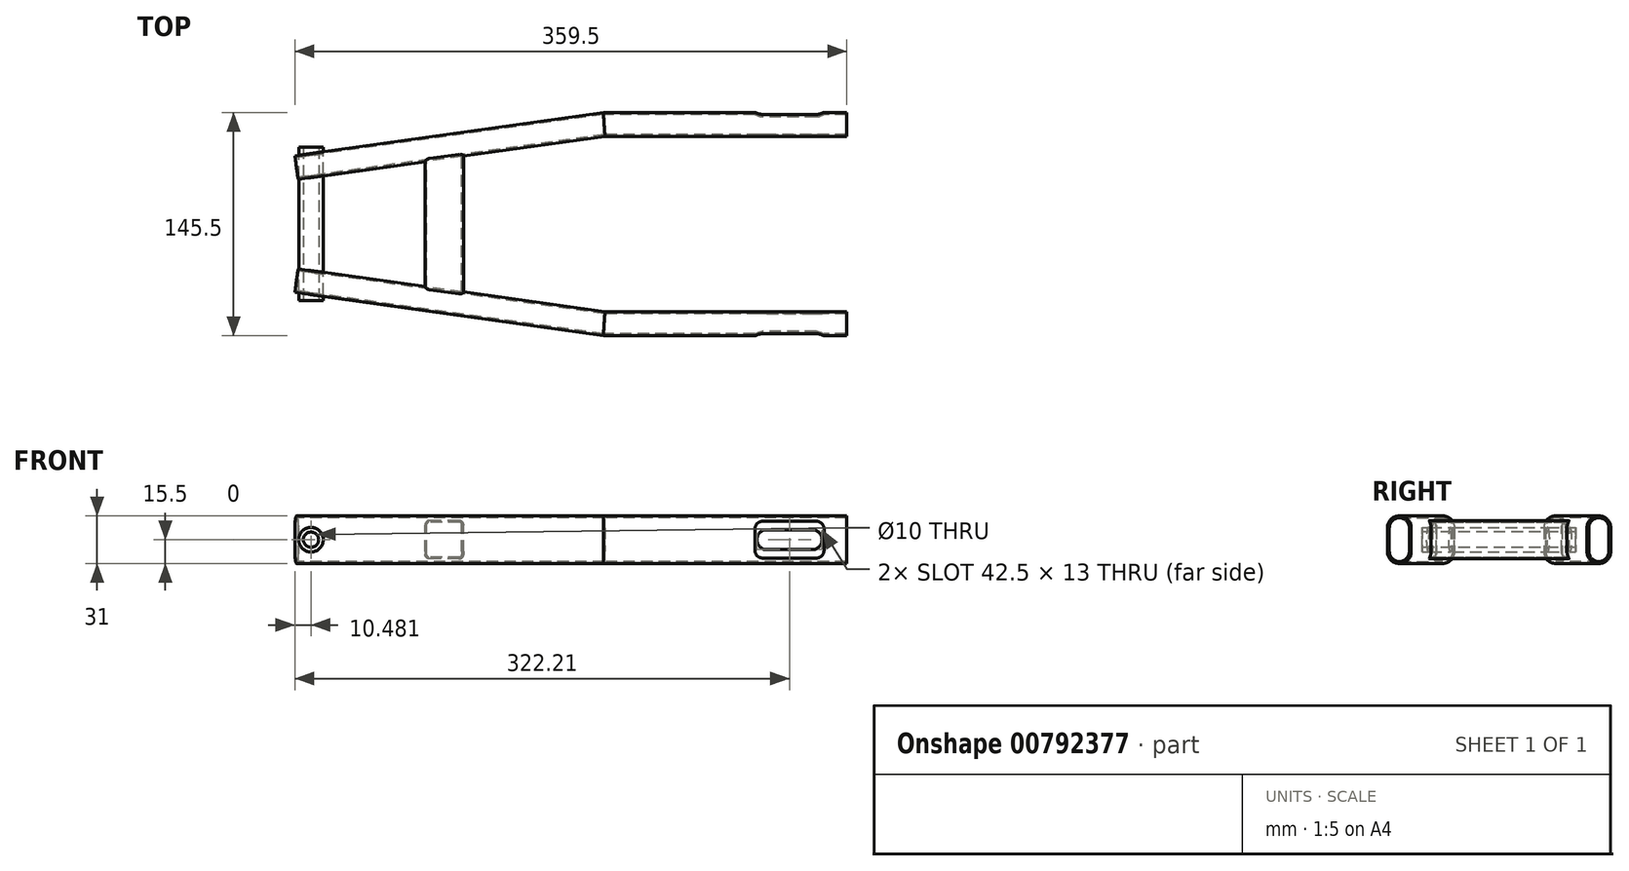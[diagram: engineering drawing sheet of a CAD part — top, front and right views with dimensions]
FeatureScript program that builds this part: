
annotation { "Feature Type Name" : "Feature", "Feature Type Description" : "" }
export const myFeature = defineFeature(function(context is Context, id is Id, definition is map)
    precondition{}
    {
        {
            var Q0;
            Q0=qCreatedBy(makeId("Top.planeOp"),FACE);
            var sketch = newSketch(context, id + "F0", { "sketchPlane" : qUnion([Q0])});
            skLineSegment(sketch, "E0", {"start": v(0, 65) * mm, "end": v(-158.03, 65) * mm});
            skLineSegment(sketch, "E1", {"start": v(-158.03, 65) * mm, "end": v(-358.42, 36.84) * mm});
            skSolve(sketch);
        }
        {
            var Q0;
            Q0=qCreatedBy(makeId("Right.planeOp"),FACE);
            var sketch = newSketch(context, id + "F1", { "sketchPlane" : qUnion([Q0])});
            skLineSegment(sketch, "E2.bottom", {"start": v(57.25, 7.75) * mm, "end": v(72.75, 7.75) * mm});
            skLineSegment(sketch, "E2.top", {"start": v(57.25, -7.75) * mm, "end": v(72.75, -7.75) * mm});
            skLineSegment(sketch, "E2.left", {"start": v(57.25, 7.75) * mm, "end": v(57.25, -7.75) * mm});
            skLineSegment(sketch, "E2.right", {"start": v(72.75, 7.75) * mm, "end": v(72.75, -7.75) * mm});
            skPoint(sketch, "E2.middle", {"position": v(65, 0) * mm});
            skArc(sketch, "E3", {"start": v(57.25, 7.75) * mm, "mid": v(65, 15.5) * mm, "end": v(72.75, 7.75) * mm});
            skArc(sketch, "E4", {"start": v(72.75, -7.75) * mm, "mid": v(65, -15.5) * mm, "end": v(57.25, -7.75) * mm});
            skLineSegment(sketch, "E5.0", {"start": v(58.45, 7.75) * mm, "end": v(58.45, -7.75) * mm});
            skLineSegment(sketch, "E6.0", {"start": v(71.55, 7.75) * mm, "end": v(71.55, -7.75) * mm});
            skArc(sketch, "E7.0", {"start": v(58.45, 7.75) * mm, "mid": v(65, 14.3) * mm, "end": v(71.55, 7.75) * mm});
            skArc(sketch, "E8.0", {"start": v(71.55, -7.75) * mm, "mid": v(65, -14.3) * mm, "end": v(58.45, -7.75) * mm});
            skSolve(sketch);
        }
        {
            var Q0;
            Q0 = qSketchRegion(id + "F1", true);
            var Q1;
            Q1 = qConstructionFilter(qBodyType(qCreatedBy(id + "F0" ,EDGE), BodyType.WIRE), ConstructionObject.NO);
            sweep(context, id + "F2", {"profiles" : qUnion([Q0]), "path" : qUnion([Q1])});
        }
        {
            var Q0;
            Q0=makeQuery(id+"F2.opSweep","SWEPT_FACE",FACE,{"disambiguationData":[OSD([sQuery(id+"F0.wireOp",EDGE,"E0"),sQuery(id+"F1.wireOp",EDGE,"E2.left")])]});
            var sketch = newSketch(context, id + "F3", { "sketchPlane" : qUnion([Q0])});
            skLineSegment(sketch, "E9.bottom", {"start": v(-22.54, -6.5) * mm, "end": v(-52.04, -6.5) * mm});
            skLineSegment(sketch, "E9.top", {"start": v(-22.54, 6.5) * mm, "end": v(-52.04, 6.5) * mm});
            skPoint(sketch, "E9.middle", {"position": v(-37.29, 0) * mm});
            skArc(sketch, "E10", {"start": v(-52.04, 6.5) * mm, "mid": v(-58.54, 0) * mm, "end": v(-52.04, -6.5) * mm});
            skArc(sketch, "E11", {"start": v(-22.54, 6.5) * mm, "mid": v(-16.04, 0) * mm, "end": v(-22.54, -6.5) * mm});
            skSolve(sketch);
        }
        {
            var Q0;
            Q0 = qSketchRegion(id + "F3", true);
            extrude(context, id + "F4", {"entities" : qUnion([Q0]), "operationType" : NewBodyOperationType.REMOVE, "oppositeDirection" : true, "depth" : 2 * mm, "offsetDistance" : 25 * mm});
        }
        {
            var Q0;
            Q0=makeQuery(id+"F2.opSweep","SWEPT_BODY",BODY,{"disambiguationData":[OSD([sQuery(id+"F0.wireOp",EDGE,"E1"),sQuery(id+"F1.wireOp",EDGE,"E2.left"),sQuery(id+"F1.wireOp",EDGE,"E2.right"),sQuery(id+"F1.wireOp",EDGE,"E3"),sQuery(id+"F1.wireOp",EDGE,"E4"),sQuery(id+"F1.wireOp",EDGE,"E5.0"),sQuery(id+"F1.wireOp",EDGE,"E6.0"),sQuery(id+"F1.wireOp",EDGE,"E7.0"),sQuery(id+"F1.wireOp",EDGE,"E8.0")])]});
            var Q1;
            Q1=qCreatedBy(makeId("Front.planeOp"),FACE);
            mirror(context, id + "F5", {"entities" : qUnion([Q0]), "mirrorPlane" : qUnion([Q1])});
        }
        {
            var Q0;
            Q0=makeQuery(id+"F5.opPattern","COPY",FACE,{"derivedFrom":makeQuery(id+"F2.opSweep","SWEPT_FACE",FACE,{"disambiguationData":[OSD([sQuery(id+"F0.wireOp",EDGE,"E0"),sQuery(id+"F1.wireOp",EDGE,"E2.right")])]}),"instanceName":"1"});
            var sketch = newSketch(context, id + "F6", { "sketchPlane" : qUnion([Q0])});
            skLineSegment(sketch, "E12.bottom", {"start": v(-19.76, 12) * mm, "end": v(-54.76, 12) * mm});
            skLineSegment(sketch, "E12.top", {"start": v(-19.76, -12) * mm, "end": v(-54.76, -12) * mm});
            skLineSegment(sketch, "E12.left", {"start": v(-14.76, 7) * mm, "end": v(-14.76, -7) * mm});
            skLineSegment(sketch, "E12.right", {"start": v(-59.76, 7) * mm, "end": v(-59.76, -7) * mm});
            skPoint(sketch, "E12.middle", {"position": v(-37.26, 0) * mm});
            skPoint(sketch, "E13.visualSharp", {"position": v(-59.76, 12) * mm});
            skArc(sketch, "E13.filletArc", {"start": v(-54.76, 12) * mm, "mid": v(-58.3, 10.54) * mm, "end": v(-59.76, 7) * mm});
            skPoint(sketch, "E14.visualSharp", {"position": v(-59.76, -12) * mm});
            skArc(sketch, "E14.filletArc", {"start": v(-59.76, -7) * mm, "mid": v(-58.3, -10.54) * mm, "end": v(-54.76, -12) * mm});
            skPoint(sketch, "E15.visualSharp", {"position": v(-14.76, -12) * mm});
            skArc(sketch, "E15.filletArc", {"start": v(-19.76, -12) * mm, "mid": v(-16.22, -10.54) * mm, "end": v(-14.76, -7) * mm});
            skPoint(sketch, "E16.visualSharp", {"position": v(-14.76, 12) * mm});
            skArc(sketch, "E16.filletArc", {"start": v(-14.76, 7) * mm, "mid": v(-16.22, 10.54) * mm, "end": v(-19.76, 12) * mm});
            skCircle(sketch, "E17", {"center": v(-349.02, 0) * mm, "radius": 8 * mm});
            skCircle(sketch, "E18", {"center": v(-349.02, 0) * mm, "radius": 5 * mm});
            skSolve(sketch);
        }
        {
            var Q0;
            {var subQ0=sQuery(id+"F6.wireOp",EDGE,"E12.bottom");Q0=makeQuery(id+"F6.imprint","IMPRINT",FACE,{"disambiguationData":[TD([[makeQuery(id+"F6.imprint","IMPRINT",EDGE,{"derivedFrom":subQ0}),1.0]])]});}
            var Q1;
            {var subQ9=sQuery(id+"F6.wireOp",EDGE,"E12.left");Q1=makeQuery(id+"F6.imprint","IMPRINT",FACE,{"disambiguationData":[TD([[makeQuery(id+"F6.imprint","IMPRINT",EDGE,{"derivedFrom":subQ9}),-1.0]])]});}
            var Q2;
            {var subQ0=sQuery(id+"F6.wireOp",EDGE,"E12.top");Q2=makeQuery(id+"F6.imprint","IMPRINT",FACE,{"disambiguationData":[TD([[makeQuery(id+"F6.imprint","IMPRINT",EDGE,{"derivedFrom":subQ0}),-1.0]])]});}
            extrude(context, id + "F7", {"entities" : qUnion([Q0, Q1, Q2]), "operationType" : NewBodyOperationType.REMOVE, "oppositeDirection" : true, "depth" : 5 * mm, "offsetDistance" : 25 * mm});
        }
        {
            var Q0;
            Q0=makeQuery(id+"F2.opSweep","SWEPT_FACE",FACE,{"disambiguationData":[OSD([sQuery(id+"F0.wireOp",EDGE,"E0"),sQuery(id+"F1.wireOp",EDGE,"E2.right")])]});
            var sketch = newSketch(context, id + "F8", { "sketchPlane" : qUnion([Q0])});
            skLineSegment(sketch, "E19.0", {"start": v(19.76, 12) * mm, "end": v(54.76, 12) * mm});
            skLineSegment(sketch, "E20.0", {"start": v(19.76, -12) * mm, "end": v(54.76, -12) * mm});
            skPoint(sketch, "E21.0", {"position": v(16.22, -10.54) * mm});
            skArc(sketch, "E22.0", {"start": v(19.76, -12) * mm, "mid": v(16.22, -10.54) * mm, "end": v(14.76, -7) * mm});
            skLineSegment(sketch, "E23.0", {"start": v(14.76, 7) * mm, "end": v(14.76, -7) * mm});
            skArc(sketch, "E24.0", {"start": v(14.76, 7) * mm, "mid": v(16.22, 10.54) * mm, "end": v(19.76, 12) * mm});
            skArc(sketch, "E25.0", {"start": v(54.76, 12) * mm, "mid": v(58.3, 10.54) * mm, "end": v(59.76, 7) * mm});
            skPoint(sketch, "E26.0", {"position": v(59.76, 0) * mm});
            skLineSegment(sketch, "E27.0", {"start": v(59.76, 7) * mm, "end": v(59.76, -7) * mm});
            skArc(sketch, "E28.0", {"start": v(59.76, -7) * mm, "mid": v(58.3, -10.54) * mm, "end": v(54.76, -12) * mm});
            skSolve(sketch);
        }
        {
            var Q0;
            Q0 = qSketchRegion(id + "F8", true);
            extrude(context, id + "F9", {"entities" : qUnion([Q0]), "operationType" : NewBodyOperationType.REMOVE, "oppositeDirection" : true, "depth" : 5 * mm, "offsetDistance" : 25 * mm});
        }
        {
            var Q0;
            Q0=qCreatedBy(makeId("Front.planeOp"),FACE);
            var sketch = newSketch(context, id + "F10", { "sketchPlane" : qUnion([Q0])});
            skCircle(sketch, "E29.0", {"center": v(-349.02, 0) * mm, "radius": 8 * mm});
            skSolve(sketch);
        }
        {
            var Q0;
            Q0 = qSketchRegion(id + "F10", true);
            extrude(context, id + "F11", {"entities" : qUnion([Q0]), "operationType" : NewBodyOperationType.ADD, "endBound" : BoundingType.SYMMETRIC, "depth" : 100 * mm, "offsetDistance" : 25 * mm});
        }
        {
            var Q0;
            Q0=makeQuery(id+"F11.opExtrude","CAP_FACE",FACE,{"disambiguationData":[OSD([sQuery(id+"F10.wireOp",EDGE,"E29.0")])],"isStart":false});
            var sketch = newSketch(context, id + "F12", { "sketchPlane" : qUnion([Q0])});
            skCircle(sketch, "E30.0", {"center": v(-349.02, 0) * mm, "radius": 5 * mm});
            skSolve(sketch);
        }
        {
            var Q0;
            Q0 = qSketchRegion(id + "F12", true);
            extrude(context, id + "F13", {"entities" : qUnion([Q0]), "operationType" : NewBodyOperationType.REMOVE, "endBound" : BoundingType.THROUGH_ALL, "oppositeDirection" : true, "depth" : 25 * mm, "offsetDistance" : 25 * mm});
        }
        {
            var Q0;
            Q0=qCreatedBy(makeId("Front.planeOp"),FACE);
            var sketch = newSketch(context, id + "F14", { "sketchPlane" : qUnion([Q0])});
            skLineSegment(sketch, "E31.bottom", {"start": v(-252.69, -12.5) * mm, "end": v(-271.69, -12.5) * mm});
            skLineSegment(sketch, "E31.top", {"start": v(-252.69, 12.5) * mm, "end": v(-271.69, 12.5) * mm});
            skLineSegment(sketch, "E31.left", {"start": v(-249.69, -9.5) * mm, "end": v(-249.69, 9.5) * mm});
            skLineSegment(sketch, "E31.right", {"start": v(-274.69, -9.5) * mm, "end": v(-274.69, 9.5) * mm});
            skPoint(sketch, "E31.middle", {"position": v(-262.19, 0) * mm});
            skLineSegment(sketch, "E32.bottom", {"start": v(-252.19, 11.4) * mm, "end": v(-272.19, 11.4) * mm});
            skLineSegment(sketch, "E32.top", {"start": v(-252.19, -11.4) * mm, "end": v(-272.19, -11.4) * mm});
            skLineSegment(sketch, "E32.left", {"start": v(-250.79, 10) * mm, "end": v(-250.79, -10) * mm});
            skLineSegment(sketch, "E32.right", {"start": v(-273.59, 10) * mm, "end": v(-273.59, -10) * mm});
            skPoint(sketch, "E33.visualSharp", {"position": v(-274.69, 12.5) * mm});
            skArc(sketch, "E33.filletArc", {"start": v(-271.69, 12.5) * mm, "mid": v(-273.81, 11.62) * mm, "end": v(-274.69, 9.5) * mm});
            skPoint(sketch, "E34.visualSharp", {"position": v(-249.69, 12.5) * mm});
            skArc(sketch, "E34.filletArc", {"start": v(-249.69, 9.5) * mm, "mid": v(-250.57, 11.62) * mm, "end": v(-252.69, 12.5) * mm});
            skPoint(sketch, "E35.visualSharp", {"position": v(-249.69, -12.5) * mm});
            skArc(sketch, "E35.filletArc", {"start": v(-252.69, -12.5) * mm, "mid": v(-250.57, -11.62) * mm, "end": v(-249.69, -9.5) * mm});
            skPoint(sketch, "E36.visualSharp", {"position": v(-274.69, -12.5) * mm});
            skArc(sketch, "E36.filletArc", {"start": v(-274.69, -9.5) * mm, "mid": v(-273.81, -11.62) * mm, "end": v(-271.69, -12.5) * mm});
            skPoint(sketch, "E37.visualSharp", {"position": v(-250.79, 11.4) * mm});
            skArc(sketch, "E37.filletArc", {"start": v(-250.79, 10) * mm, "mid": v(-251.2, 10.99) * mm, "end": v(-252.19, 11.4) * mm});
            skPoint(sketch, "E38.visualSharp", {"position": v(-250.79, -11.4) * mm});
            skArc(sketch, "E38.filletArc", {"start": v(-252.19, -11.4) * mm, "mid": v(-251.2, -10.99) * mm, "end": v(-250.79, -10) * mm});
            skPoint(sketch, "E39.visualSharp", {"position": v(-273.59, -11.4) * mm});
            skArc(sketch, "E39.filletArc", {"start": v(-273.59, -10) * mm, "mid": v(-273.18, -10.99) * mm, "end": v(-272.19, -11.4) * mm});
            skPoint(sketch, "E40.visualSharp", {"position": v(-273.59, 11.4) * mm});
            skArc(sketch, "E40.filletArc", {"start": v(-272.19, 11.4) * mm, "mid": v(-273.18, 10.99) * mm, "end": v(-273.59, 10) * mm});
            skSolve(sketch);
        }
        {
            var Q0;
            Q0 = qSketchRegion(id + "F14", true);
            extrude(context, id + "F15", {"entities" : qUnion([Q0]), "operationType" : NewBodyOperationType.ADD, "endBound" : BoundingType.UP_TO_NEXT, "depth" : 25 * mm, "offsetDistance" : 25 * mm, "hasSecondDirection" : true, "secondDirectionBound" : SecondDirectionBoundingType.UP_TO_NEXT, "secondDirectionOppositeDirection" : true, "secondDirectionDepth" : 25 * mm});
        }
    });
